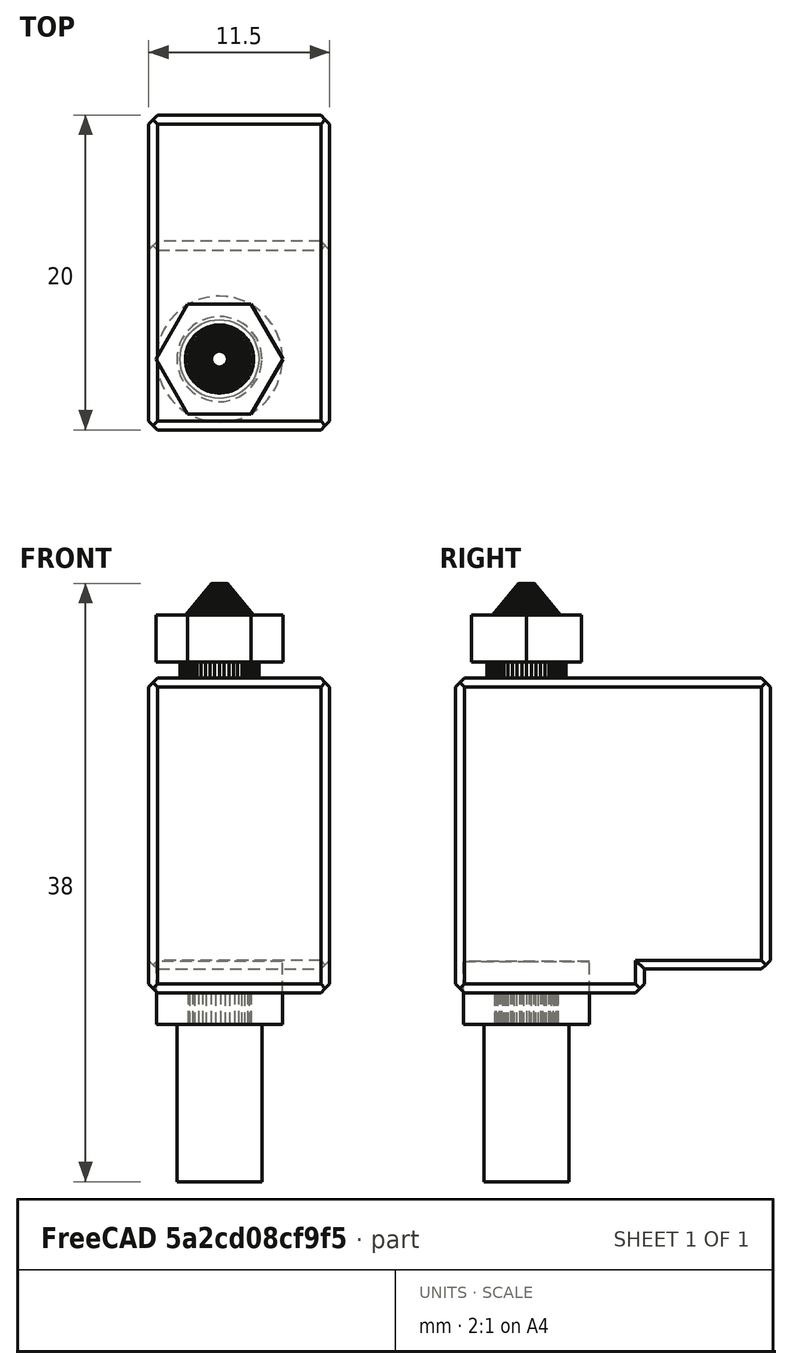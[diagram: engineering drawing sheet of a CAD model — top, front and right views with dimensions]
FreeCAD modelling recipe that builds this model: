
FCSTD DOCUMENT  (FreeCAD 0.18R16146 (Git))
Label: volcano-hotend
License: All rights reserved
LicenseURL: http://en.wikipedia.org/wiki/All_rights_reserved
objects: Part::Feature×3, Part::Cylinder×2, Mesh::Feature×1, Part::Box×1, Part::Cut×1
note: 7 computed .brp shape members not serialized (recipe doc carries the construction recipe); baked Part::Feature solids carry a one-line shape summary decoded from their .brp

FEATURE [Mesh::Feature] e3d_v6_volcano_all_metall_hotend_coarse
FEATURE [Part::Feature] e3d_v6_volcano_all_metall_hotend_coarse001
  shape: bbox 22.3 x 26.65 x 74.1 mm, 3592 faces, 0 solids (baked)
FEATURE [Part::Feature] e3d_v6_volcano_all_metall_hotend_coarse001001  label="e3d_v6_volcano_all_metall_hotend_coarse002"
  shape: bbox 22.3 x 26.65 x 74.1 mm, 1020 faces, 0 solids (baked)
FEATURE [Part::Feature] e3d_v6_volcano_all_metall_hotend_coarse001001_solid  label="e3d_v6_volcano_all_metall_hotend_coarse002 (Solid)"
  shape: bbox 22.3 x 26.65 x 74.1 mm, 1020 faces (baked)
FEATURE [Part::Box] Box  label="Cube"
  AttacherType = Attacher::AttachEngine3D
  Height = 50
  Length = 28
  Placement = pos=(-14.4,-15.2,-3.9) rot=(0,0,1;0rad)
  Width = 30
FEATURE [Part::Cut] Cut
  Base = -> e3d_v6_volcano_all_metall_hotend_coarse001001_solid
  Placement = pos=(0,0,-36.1) rot=(0,0,1;0rad)
  Tool = -> Box
FEATURE [Part::Cylinder] Cylinder
  Angle = 360
  AttacherType = Attacher::AttachEngine3D
  Height = 10
  Radius = 2.7
FEATURE [Part::Cylinder] Cylinder001
  Angle = 360
  AttacherType = Attacher::AttachEngine3D
  Height = 4
  Placement = pos=(0,0,10) rot=(0,0,1;0rad)
  Radius = 4
